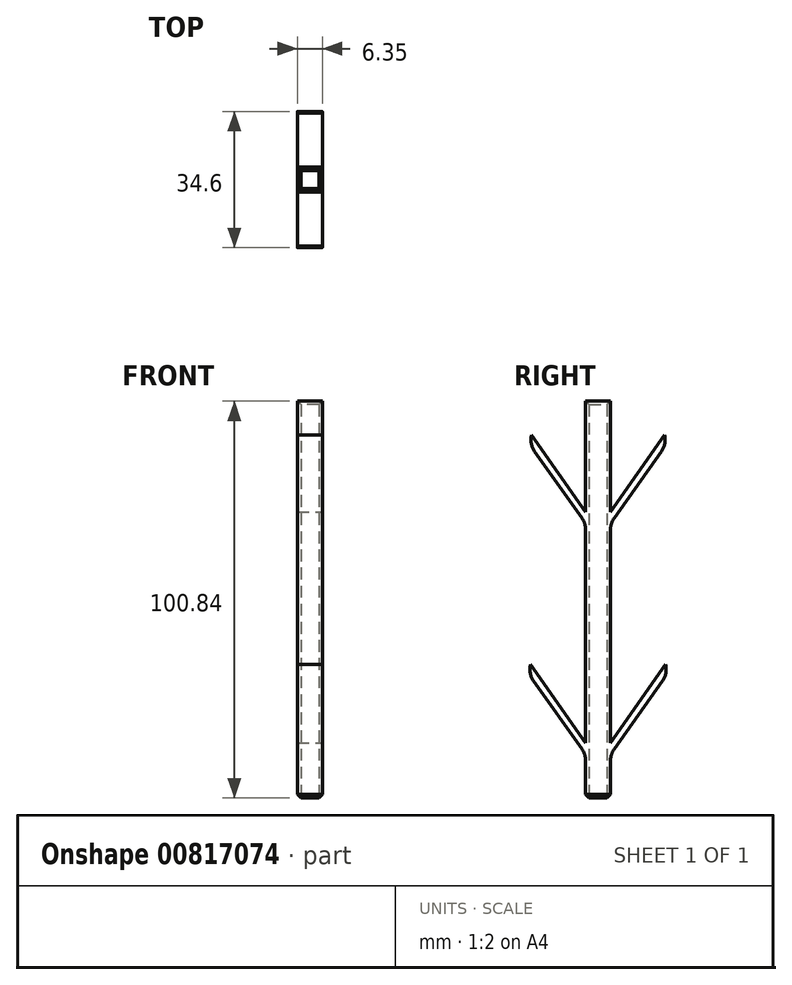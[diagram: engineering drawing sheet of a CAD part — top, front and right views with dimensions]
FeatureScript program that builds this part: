
annotation { "Feature Type Name" : "Feature", "Feature Type Description" : "" }
export const myFeature = defineFeature(function(context is Context, id is Id, definition is map)
    precondition{}
    {
        {
            var Q0;
            Q0=qCreatedBy(makeId("Top.planeOp"),FACE);
            var sketch = newSketch(context, id + "F0", { "sketchPlane" : qUnion([Q0])});
            skLineSegment(sketch, "E0.bottom", {"start": v(2.29, 2.29) * mm, "end": v(-2.29, 2.29) * mm});
            skLineSegment(sketch, "E0.top", {"start": v(2.29, -2.29) * mm, "end": v(-2.29, -2.29) * mm});
            skLineSegment(sketch, "E0.left", {"start": v(2.29, 2.29) * mm, "end": v(2.29, -2.29) * mm});
            skLineSegment(sketch, "E0.right", {"start": v(-2.29, 2.29) * mm, "end": v(-2.29, -2.29) * mm});
            skPoint(sketch, "E0.middle", {"position": v(0, 0) * mm});
            skLineSegment(sketch, "E1.bottom", {"start": v(3.18, 3.18) * mm, "end": v(-3.18, 3.17) * mm});
            skLineSegment(sketch, "E1.top", {"start": v(3.18, -3.17) * mm, "end": v(-3.18, -3.18) * mm});
            skLineSegment(sketch, "E1.left", {"start": v(3.18, 3.18) * mm, "end": v(3.18, -3.17) * mm});
            skLineSegment(sketch, "E1.right", {"start": v(-3.18, 3.17) * mm, "end": v(-3.18, -3.18) * mm});
            skSolve(sketch);
        }
        {
            var Q0;
            Q0 = qSketchRegion(id + "F0", true);
            extrude(context, id + "F1", {"entities" : qUnion([Q0]), "endBound" : BoundingType.SYMMETRIC, "depth" : 101.6 * mm, "offsetDistance" : 25.4 * mm});
        }
        {
            var Q0;
            Q0=qCreatedBy(makeId("Right.planeOp"),FACE);
            var sketch = newSketch(context, id + "F2", { "sketchPlane" : qUnion([Q0])});
            skLineSegment(sketch, "E2", {"start": v(-2.84, -39.73) * mm, "end": v(-19.35, -16.51) * mm});
            skLineSegment(sketch, "E3", {"start": v(-19.35, -16.51) * mm, "end": v(-17.14, -16.51) * mm});
            skLineSegment(sketch, "E4", {"start": v(-17.14, -16.51) * mm, "end": v(-2.6, -37.28) * mm});
            skLineSegment(sketch, "E5", {"start": v(-2.6, -37.28) * mm, "end": v(-2.84, -39.73) * mm});
            skLineSegment(sketch, "E6", {"start": v(-2.6, 18.64) * mm, "end": v(-19.1, 41.86) * mm});
            skLineSegment(sketch, "E7", {"start": v(-19.1, 41.86) * mm, "end": v(-16.9, 41.86) * mm});
            skLineSegment(sketch, "E8", {"start": v(-16.9, 41.86) * mm, "end": v(-2.35, 21.09) * mm});
            skLineSegment(sketch, "E9", {"start": v(-2.35, 21.09) * mm, "end": v(-2.6, 18.64) * mm});
            skLineSegment(sketch, "E10", {"start": v(0, 66.84) * mm, "end": v(0, -62.55) * mm});
            skLineSegment(sketch, "E11.MirrorCS", {"start": v(19.1, 41.86) * mm, "end": v(16.9, 41.86) * mm});
            skLineSegment(sketch, "E12.MirrorCS", {"start": v(2.35, 21.09) * mm, "end": v(2.6, 18.64) * mm});
            skLineSegment(sketch, "E13.MirrorCS", {"start": v(16.9, 41.86) * mm, "end": v(2.35, 21.09) * mm});
            skLineSegment(sketch, "E14.MirrorCS", {"start": v(2.6, 18.64) * mm, "end": v(19.1, 41.86) * mm});
            skLineSegment(sketch, "E15.MirrorCS", {"start": v(2.6, -37.28) * mm, "end": v(2.84, -39.73) * mm});
            skLineSegment(sketch, "E16.MirrorCS", {"start": v(19.35, -16.51) * mm, "end": v(17.14, -16.51) * mm});
            skLineSegment(sketch, "E17.MirrorCS", {"start": v(2.84, -39.73) * mm, "end": v(19.35, -16.51) * mm});
            skLineSegment(sketch, "E18.MirrorCS", {"start": v(17.14, -16.51) * mm, "end": v(2.6, -37.28) * mm});
            skSolve(sketch);
        }
        {
            var Q0;
            Q0=makeQuery(id+"F1.opExtrude","CAP_EDGE",EDGE,{"disambiguationData":[OSD([sQuery(id+"F0.wireOp",EDGE,"E0.bottom")])],"isStart":false});
            var Q1;
            Q1=makeQuery(id+"F1.opExtrude","CAP_EDGE",EDGE,{"disambiguationData":[OSD([sQuery(id+"F0.wireOp",EDGE,"E0.right")])],"isStart":false});
            var Q2;
            Q2=makeQuery(id+"F1.opExtrude","CAP_EDGE",EDGE,{"disambiguationData":[OSD([sQuery(id+"F0.wireOp",EDGE,"E0.top")])],"isStart":false});
            var Q3;
            Q3=makeQuery(id+"F1.opExtrude","CAP_EDGE",EDGE,{"disambiguationData":[OSD([sQuery(id+"F0.wireOp",EDGE,"E0.left")])],"isStart":false});
            chamfer(context, id + "F3", {"entities" : qUnion([Q0, Q1, Q2, Q3]), "width" : 1.27 * mm, "tangentPropagation" : true});
        }
        {
            var Q0;
            Q0=makeQuery(id+"F1.opExtrude","CAP_EDGE",EDGE,{"disambiguationData":[OSD([sQuery(id+"F0.wireOp",EDGE,"E1.left")])],"isStart":true});
            var Q1;
            Q1=makeQuery(id+"F1.opExtrude","CAP_EDGE",EDGE,{"disambiguationData":[OSD([sQuery(id+"F0.wireOp",EDGE,"E1.top")])],"isStart":true});
            var Q2;
            Q2=makeQuery(id+"F1.opExtrude","CAP_EDGE",EDGE,{"disambiguationData":[OSD([sQuery(id+"F0.wireOp",EDGE,"E1.right")])],"isStart":true});
            var Q3;
            Q3=makeQuery(id+"F1.opExtrude","CAP_EDGE",EDGE,{"disambiguationData":[OSD([sQuery(id+"F0.wireOp",EDGE,"E1.bottom")])],"isStart":true});
            chamfer(context, id + "F4", {"entities" : qUnion([Q0, Q1, Q2, Q3]), "width" : 1.27 * mm, "tangentPropagation" : true});
        }
        {
            var Q0;
            Q0=makeQuery(id+"F2.imprint","IMPRINT",FACE,{"disambiguationData":[TD([[makeQuery(id+"F2.imprint","IMPRINT",EDGE,{"derivedFrom":sQuery(id+"F2.wireOp",EDGE,"E6")}),-1.0]])]});
            var Q1;
            Q1=makeQuery(id+"F2.imprint","IMPRINT",FACE,{"disambiguationData":[TD([[makeQuery(id+"F2.imprint","IMPRINT",EDGE,{"derivedFrom":sQuery(id+"F2.wireOp",EDGE,"E2")}),-1.0]])]});
            var Q2;
            Q2=makeQuery(id+"F2.imprint","IMPRINT",FACE,{"disambiguationData":[TD([[makeQuery(id+"F2.imprint","IMPRINT",EDGE,{"derivedFrom":sQuery(id+"F2.wireOp",EDGE,"E11.MirrorCS")}),1.0]])]});
            var Q3;
            Q3=makeQuery(id+"F2.imprint","IMPRINT",FACE,{"disambiguationData":[TD([[makeQuery(id+"F2.imprint","IMPRINT",EDGE,{"derivedFrom":sQuery(id+"F2.wireOp",EDGE,"E15.MirrorCS")}),1.0]])]});
            extrude(context, id + "F5", {"entities" : qUnion([Q0, Q1, Q2, Q3]), "operationType" : NewBodyOperationType.ADD, "endBound" : BoundingType.SYMMETRIC, "depth" : 6.35 * mm, "offsetDistance" : 25.4 * mm});
        }
        {
            var Q0;
            Q0=makeQuery(id+"F5.boolean.opBoolean","INTERSECT",EDGE,{"derivedFrom":[makeQuery(id+"F1.opExtrude","SWEPT_FACE",FACE,{"disambiguationData":[OSD([sQuery(id+"F0.wireOp",EDGE,"E1.top")])]}),makeQuery(id+"F5.opExtrude","SWEPT_FACE",FACE,{"disambiguationData":[OSD([sQuery(id+"F2.wireOp",EDGE,"E6")])]})]});
            var Q1;
            Q1=makeQuery(id+"F5.opExtrude","SWEPT_EDGE",EDGE,{"disambiguationData":[OSD([sQuery(id+"F2.wireOp",EDGE,"E6"),sQuery(id+"F2.wireOp",EDGE,"E7")])]});
            var Q2;
            Q2=makeQuery(id+"F5.boolean.opBoolean","INTERSECT",EDGE,{"derivedFrom":[makeQuery(id+"F1.opExtrude","SWEPT_FACE",FACE,{"disambiguationData":[OSD([sQuery(id+"F0.wireOp",EDGE,"E1.top")])]}),makeQuery(id+"F5.opExtrude","SWEPT_FACE",FACE,{"disambiguationData":[OSD([sQuery(id+"F2.wireOp",EDGE,"E2")])]})]});
            var Q3;
            Q3=makeQuery(id+"F5.opExtrude","SWEPT_EDGE",EDGE,{"disambiguationData":[OSD([sQuery(id+"F2.wireOp",EDGE,"E2"),sQuery(id+"F2.wireOp",EDGE,"E3")])]});
            var Q4;
            Q4=makeQuery(id+"F5.opExtrude","SWEPT_EDGE",EDGE,{"disambiguationData":[OSD([sQuery(id+"F2.wireOp",EDGE,"E16.MirrorCS"),sQuery(id+"F2.wireOp",EDGE,"E17.MirrorCS")])]});
            var Q5;
            Q5=makeQuery(id+"F5.boolean.opBoolean","INTERSECT",EDGE,{"derivedFrom":[makeQuery(id+"F1.opExtrude","SWEPT_FACE",FACE,{"disambiguationData":[OSD([sQuery(id+"F0.wireOp",EDGE,"E1.bottom")])]}),makeQuery(id+"F5.opExtrude","SWEPT_FACE",FACE,{"disambiguationData":[OSD([sQuery(id+"F2.wireOp",EDGE,"E17.MirrorCS")])]})]});
            var Q6;
            Q6=makeQuery(id+"F5.boolean.opBoolean","INTERSECT",EDGE,{"derivedFrom":[makeQuery(id+"F1.opExtrude","SWEPT_FACE",FACE,{"disambiguationData":[OSD([sQuery(id+"F0.wireOp",EDGE,"E1.bottom")])]}),makeQuery(id+"F5.opExtrude","SWEPT_FACE",FACE,{"disambiguationData":[OSD([sQuery(id+"F2.wireOp",EDGE,"E14.MirrorCS")])]})]});
            var Q7;
            Q7=makeQuery(id+"F5.opExtrude","SWEPT_EDGE",EDGE,{"disambiguationData":[OSD([sQuery(id+"F2.wireOp",EDGE,"E11.MirrorCS"),sQuery(id+"F2.wireOp",EDGE,"E14.MirrorCS")])]});
            fillet(context, id + "F6", {"entities" : qUnion([Q0, Q1, Q2, Q3, Q4, Q5, Q6, Q7]), "radius" : 5.08 * mm, "tangentPropagation" : true, "allowEdgeOverflow" : false});
        }
    });
